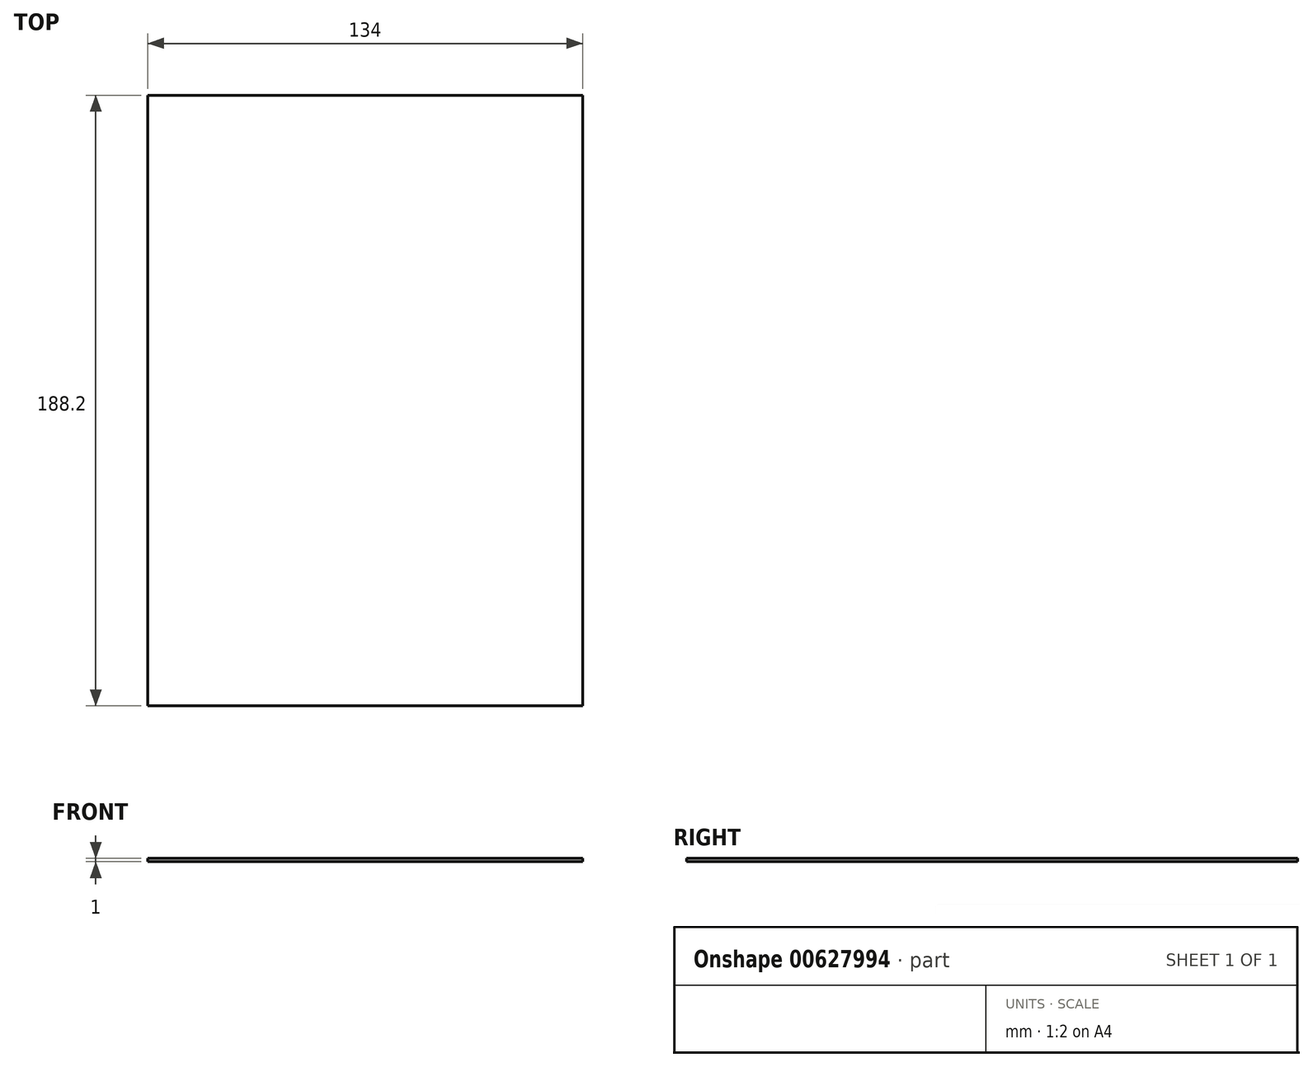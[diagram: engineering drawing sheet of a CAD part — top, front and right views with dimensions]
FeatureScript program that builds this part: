
annotation { "Feature Type Name" : "Feature", "Feature Type Description" : "" }
export const myFeature = defineFeature(function(context is Context, id is Id, definition is map)
    precondition{}
    {
        {
            var Q0;
            Q0=qCreatedBy(makeId("Top.planeOp"),FACE);
            var sketch = newSketch(context, id + "F0", { "sketchPlane" : qUnion([Q0])});
            skLineSegment(sketch, "E0.bottom", {"start": v(0, 0) * mm, "end": v(134, 0) * mm});
            skLineSegment(sketch, "E0.top", {"start": v(0, 188.2) * mm, "end": v(134, 188.2) * mm});
            skLineSegment(sketch, "E0.left", {"start": v(0, 0) * mm, "end": v(0, 188.2) * mm});
            skLineSegment(sketch, "E0.right", {"start": v(134, 0) * mm, "end": v(134, 188.2) * mm});
            skSolve(sketch);
        }
        {
            var Q0;
            Q0 = qSketchRegion(id + "F0", true);
            extrude(context, id + "F1", {"entities" : qUnion([Q0]), "depth" : 1 * mm, "offsetDistance" : 25 * mm});
        }
    });
